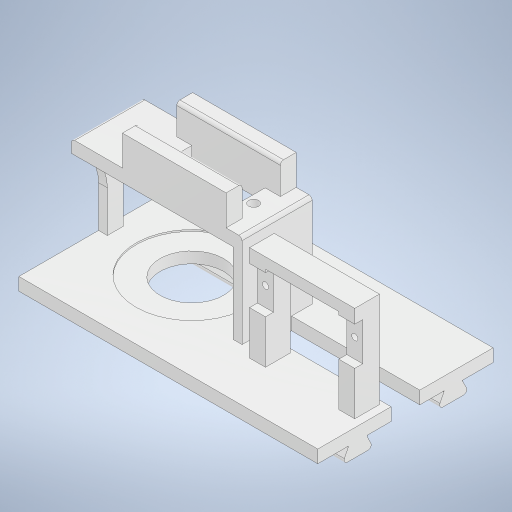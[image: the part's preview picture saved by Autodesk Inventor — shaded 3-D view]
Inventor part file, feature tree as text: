
AUTODESK INVENTOR PART (.ipt)
format: ipt  version: 2023 (Build 270158000, 158)  size: 449,536 bytes
history: mixed  units: in
note: dims shown in document units (in); Inventor stores cm internally (conversion verified against a paired STEP export)
features: move_body x3, sketch x2, hole x2, extrude x1, plane x1, imported_body x1
ambient origin geometry x8: Origin, YZ Plane, XZ Plane, XY Plane, X Axis, Y Axis, Z Axis, Center Point
bodies: Solid1 (imported_parasolid), Body17 (imported_parasolid)
feature tree (10):
  extrude  "Extrusion1"  Depth=1.378in
  plane  "Arbeitsebene1"
  sketch  "Skizze2"  dims[d6=0.3937in d7=0.0in d8=1.5625in d10=0.0945in d11=0.126in d12=0.126in d13=0.2362in d14=0.248in d15=0.0787in d16=0.6181in d17=0.315in d18=0.8108in d19=0.126in d20=0.2362in d21=0.2559in d22=0.0945in d23=90.0deg d24=0.315in d25=0.8108in d26=90.0deg d27=2.7559in d28=0.0in d29=0.3937in d30=0.1969in d31=0.0in d32=0.0in]
  hole  "Bohrung1"  [1 undecoded]
  hole  "Bohrung2"  [1 undecoded]
  move_body  "Move Body1"
  move_body  "Move Body2"
  move_body  "Move Body3"
  sketch  "Skizze1"  dims[d0=1.378in d1=0.7874in]
  imported_body  NMx_Import_Brep_tag  [imported B-rep: ~85 faces, bbox_mm=[93.75, 46.907349, 55.000001]]
note: 2 required parameter values undecoded (feature->parameter linkage not recoverable at this tier; creation-order binding heuristic only, values carry confidence <= 0.55)
